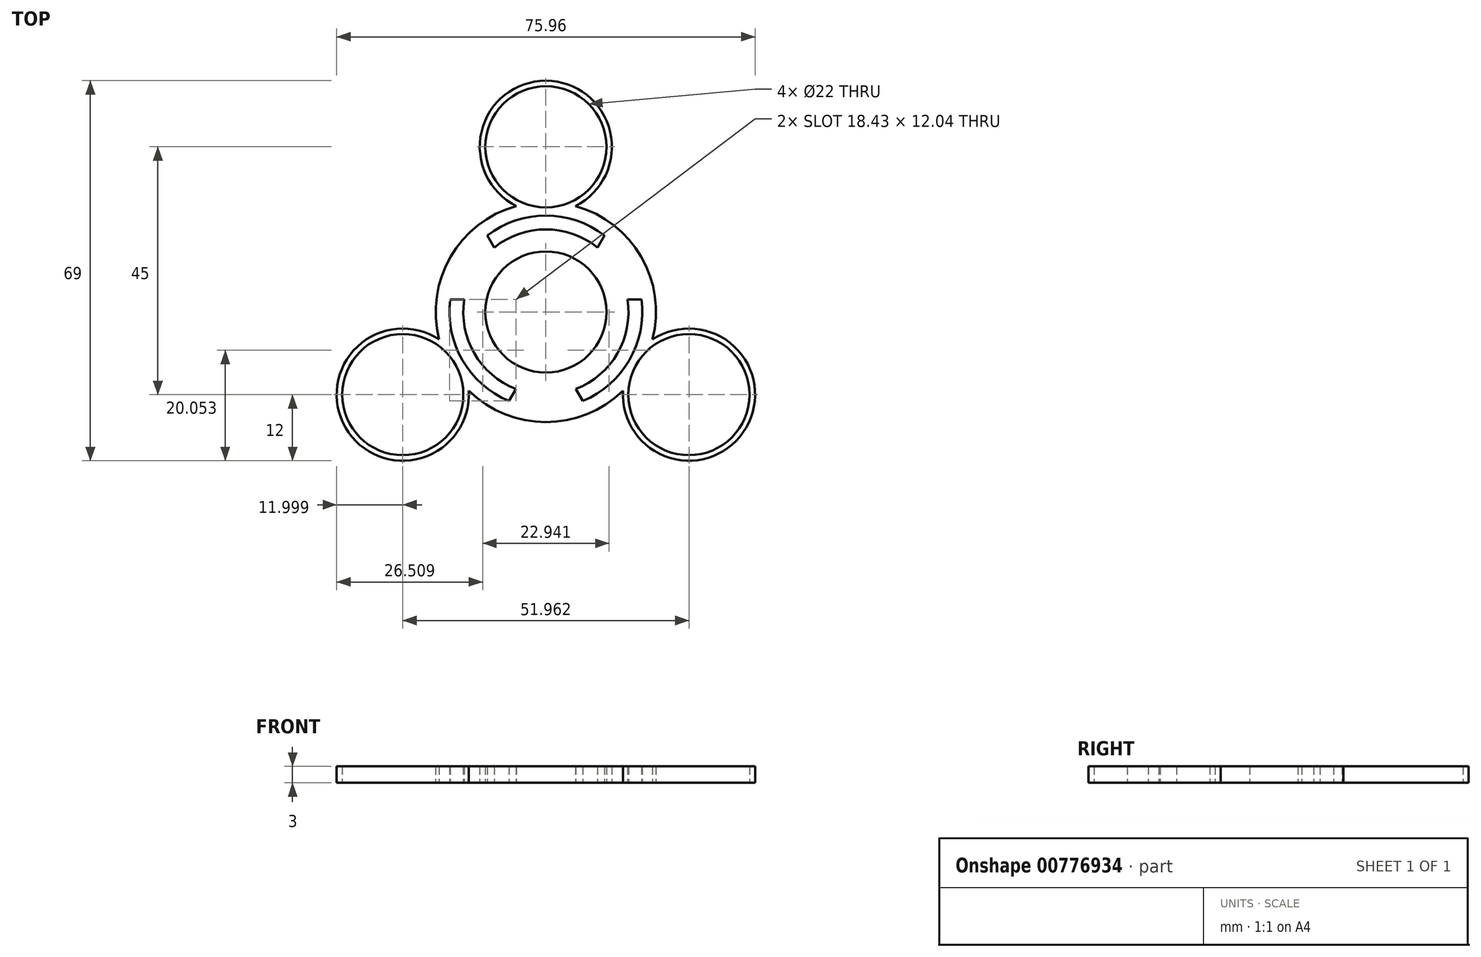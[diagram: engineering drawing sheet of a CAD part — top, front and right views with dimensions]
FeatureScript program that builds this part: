
annotation { "Feature Type Name" : "Feature", "Feature Type Description" : "" }
export const myFeature = defineFeature(function(context is Context, id is Id, definition is map)
    precondition{}
    {
        {
            var Q0;
            Q0=qCreatedBy(makeId("Top.planeOp"),FACE);
            var sketch = newSketch(context, id + "F0", { "sketchPlane" : qUnion([Q0])});
            skArc(sketch, "E0", {"start": v(11, 0) * mm, "mid": v(0, 11) * mm, "end": v(-11, 0) * mm});
            skArc(sketch, "E1", {"start": v(20, 0) * mm, "mid": v(15.93, 12.1) * mm, "end": v(5.37, 19.27) * mm});
            skArc(sketch, "E2", {"start": v(9.38, 11.7) * mm, "mid": v(0, 15) * mm, "end": v(-9.38, 11.7) * mm});
            skArc(sketch, "E3", {"start": v(10.64, 13.9) * mm, "mid": v(0, 17.5) * mm, "end": v(-10.64, 13.9) * mm});
            skLineSegment(sketch, "E4", {"start": v(-17.35, 2.27) * mm, "end": v(-14.83, 2.27) * mm});
            skLineSegment(sketch, "E5.trimOffspring", {"start": v(14.83, 2.27) * mm, "end": v(17.35, 2.27) * mm});
            skCircle(sketch, "E6", {"center": v(0, 30) * mm, "radius": 11 * mm});
            skArc(sketch, "E7", {"start": v(5.37, 19.27) * mm, "mid": v(0, 42) * mm, "end": v(-5.37, 19.27) * mm});
            skArc(sketch, "E8.trimOffspring", {"start": v(-5.37, 19.27) * mm, "mid": v(-15.93, 12.1) * mm, "end": v(-20, 0) * mm});
            skArc(sketch, "E9.1.0", {"start": v(-10, 17.32) * mm, "mid": v(-18.44, 7.74) * mm, "end": v(-19.37, -4.99) * mm});
            skArc(sketch, "E9.1.1", {"start": v(-5.5, 9.53) * mm, "mid": v(-9.53, -5.5) * mm, "end": v(5.5, -9.53) * mm});
            skArc(sketch, "E9.1.2", {"start": v(-19.37, -4.99) * mm, "mid": v(-36.37, -21) * mm, "end": v(-14, -14.28) * mm});
            skCircle(sketch, "E9.1.4", {"center": v(-25.98, -15) * mm, "radius": 11 * mm});
            skArc(sketch, "E9.1.5", {"start": v(-14, -14.28) * mm, "mid": v(-2.51, -19.84) * mm, "end": v(10, -17.32) * mm});
            skArc(sketch, "E9.1.8", {"start": v(-14.83, 2.27) * mm, "mid": v(-13, -7.5) * mm, "end": v(-5.45, -13.97) * mm});
            skArc(sketch, "E9.1.9", {"start": v(-17.35, 2.27) * mm, "mid": v(-15.16, -8.75) * mm, "end": v(-6.71, -16.16) * mm});
            skLineSegment(sketch, "E9.1.10", {"start": v(6.71, -16.16) * mm, "end": v(5.45, -13.97) * mm});
            skLineSegment(sketch, "E9.1.11", {"start": v(-9.38, 11.7) * mm, "end": v(-10.64, 13.9) * mm});
            skArc(sketch, "E9.2.0", {"start": v(-10, -17.32) * mm, "mid": v(2.51, -19.84) * mm, "end": v(14, -14.28) * mm});
            skArc(sketch, "E9.2.1", {"start": v(-5.5, -9.53) * mm, "mid": v(9.53, -5.5) * mm, "end": v(5.5, 9.53) * mm});
            skArc(sketch, "E9.2.2", {"start": v(14, -14.28) * mm, "mid": v(36.37, -21) * mm, "end": v(19.37, -4.99) * mm});
            skCircle(sketch, "E9.2.4", {"center": v(25.98, -15) * mm, "radius": 11 * mm});
            skArc(sketch, "E9.2.5", {"start": v(19.37, -4.99) * mm, "mid": v(18.44, 7.74) * mm, "end": v(10, 17.32) * mm});
            skArc(sketch, "E9.2.8", {"start": v(5.45, -13.97) * mm, "mid": v(13, -7.5) * mm, "end": v(14.83, 2.27) * mm});
            skArc(sketch, "E9.2.9", {"start": v(6.71, -16.16) * mm, "mid": v(15.16, -8.75) * mm, "end": v(17.35, 2.27) * mm});
            skLineSegment(sketch, "E9.2.10", {"start": v(10.64, 13.9) * mm, "end": v(9.38, 11.7) * mm});
            skLineSegment(sketch, "E9.2.11", {"start": v(-5.45, -13.97) * mm, "end": v(-6.71, -16.16) * mm});
            skPoint(sketch, "E10.orphan", {"position": v(-17.04, 29.5) * mm});
            skPoint(sketch, "E11.orphan", {"position": v(20.33, -35.21) * mm});
            skPoint(sketch, "E12.orphan", {"position": v(-17.04, -29.5) * mm});
            skPoint(sketch, "E13.orphan", {"position": v(34.07, 0) * mm});
            skSolve(sketch);
        }
        {
            var Q0;
            Q0 = qSketchRegion(id + "F0", true);
            extrude(context, id + "F1", {"entities" : qUnion([Q0]), "depth" : 3 * mm, "offsetDistance" : 25 * mm});
        }
    });
